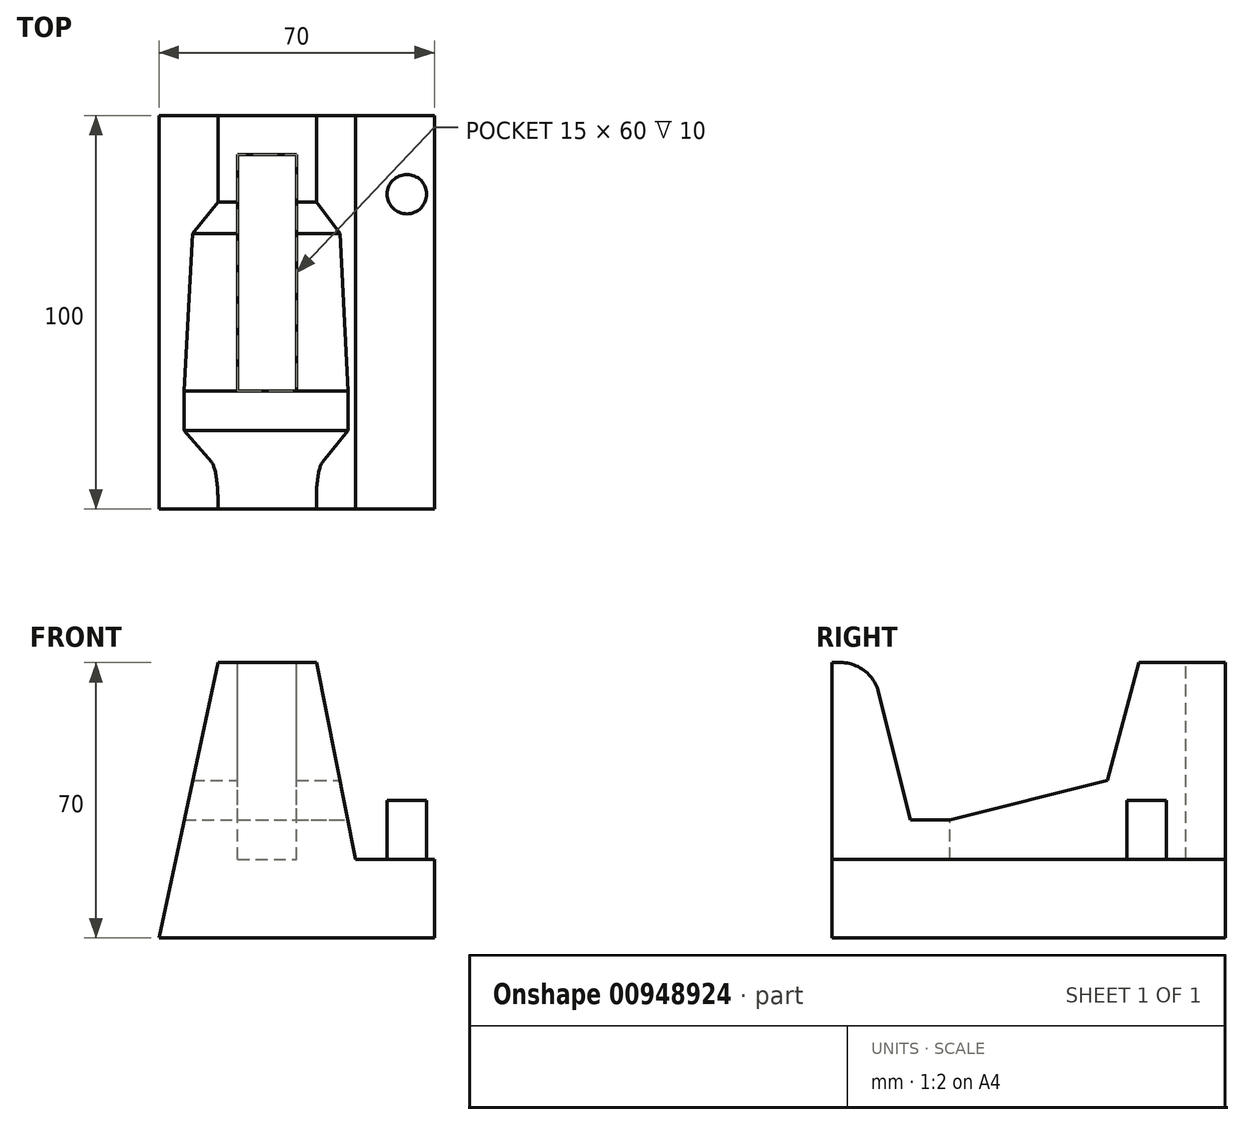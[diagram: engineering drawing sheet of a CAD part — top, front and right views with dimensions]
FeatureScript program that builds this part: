
annotation { "Feature Type Name" : "Feature", "Feature Type Description" : "" }
export const myFeature = defineFeature(function(context is Context, id is Id, definition is map)
    precondition{}
    {
        {
            var Q0;
            Q0=qCreatedBy(makeId("Front.planeOp"),FACE);
            var sketch = newSketch(context, id + "F0", { "sketchPlane" : qUnion([Q0])});
            skLineSegment(sketch, "E0", {"start": v(0, 0) * mm, "end": v(15, 70) * mm});
            skLineSegment(sketch, "E1", {"start": v(15, 70) * mm, "end": v(40, 70) * mm});
            skLineSegment(sketch, "E2", {"start": v(40, 70) * mm, "end": v(50, 20) * mm});
            skLineSegment(sketch, "E3", {"start": v(50, 20) * mm, "end": v(70, 20) * mm});
            skLineSegment(sketch, "E4", {"start": v(70, 20) * mm, "end": v(70, 0) * mm});
            skLineSegment(sketch, "E5", {"start": v(70, 0) * mm, "end": v(0, 0) * mm});
            skSolve(sketch);
        }
        {
            var Q0;
            Q0 = qSketchRegion(id + "F0", true);
            extrude(context, id + "F1", {"entities" : qUnion([Q0]), "oppositeDirection" : true, "depth" : 100 * mm, "offsetDistance" : 25 * mm});
        }
        {
            var Q0;
            Q0=makeQuery(id+"F1.opExtrude","SWEPT_FACE",FACE,{"disambiguationData":[OSD([sQuery(id+"F0.wireOp",EDGE,"E4")])]});
            var sketch = newSketch(context, id + "F2", { "sketchPlane" : qUnion([Q0])});
            skPoint(sketch, "E6.startSnap0", {"position": v(0, 10) * mm});
            skLineSegment(sketch, "E7", {"start": v(10, 70) * mm, "end": v(20, 30) * mm});
            skLineSegment(sketch, "E8", {"start": v(20, 30) * mm, "end": v(30, 30) * mm});
            skLineSegment(sketch, "E9", {"start": v(30, 30) * mm, "end": v(70, 40) * mm});
            skLineSegment(sketch, "E10", {"start": v(70, 40) * mm, "end": v(78.04, 70) * mm});
            skLineSegment(sketch, "E11", {"start": v(78.04, 70) * mm, "end": v(10, 70) * mm});
            skLineSegment(sketch, "E12", {"start": v(70, 40) * mm, "end": v(70, 70) * mm, "construction": true});
            skSolve(sketch);
        }
        {
            var Q0;
            Q0 = qSketchRegion(id + "F2", true);
            extrude(context, id + "F3", {"entities" : qUnion([Q0]), "operationType" : NewBodyOperationType.REMOVE, "endBound" : BoundingType.THROUGH_ALL, "oppositeDirection" : true, "depth" : 25 * mm, "offsetDistance" : 25 * mm});
        }
        {
            var Q0;
            Q0=makeQuery(id+"F3.boolean.opBoolean","COPY",EDGE,{"derivedFrom":makeQuery(id+"F3.opExtrude","SWEPT_EDGE",EDGE,{"disambiguationData":[OSD([sQuery(id+"F2.wireOp",EDGE,"E7"),sQuery(id+"F2.wireOp",EDGE,"E11")])]})});
            var Q1;
            Q1=makeQuery(id+"F3.boolean.opBoolean","COPY",EDGE,{"derivedFrom":makeQuery(id+"F3.opExtrude","SWEPT_EDGE",EDGE,{"disambiguationData":[OSD([sQuery(id+"F2.wireOp",EDGE,"E10"),sQuery(id+"F2.wireOp",EDGE,"E11")])]})});
            fillet(context, id + "F4", {"entities" : qUnion([Q0, Q1]), "radius" : 10 * mm, "tangentPropagation" : true, "allowEdgeOverflow" : false});
        }
        {
            var Q0;
            {var subQ2=sQuery(id+"F0.wireOp",EDGE,"E1");Q0=makeQuery(id+"F3.boolean.opBoolean","SPLIT",FACE,{"disambiguationData":[TD([makeQuery(id+"F3.opExtrude","SWEPT_FACE",FACE,{"disambiguationData":[OSD([sQuery(id+"F2.wireOp",EDGE,"E10")])]})])],"derivedFrom":makeQuery(id+"F1.opExtrude","SWEPT_FACE",FACE,{"disambiguationData":[OSD([subQ2])]})});}
            var sketch = newSketch(context, id + "F5", { "sketchPlane" : qUnion([Q0])});
            skPoint(sketch, "E13.firstSnap0", {"position": v(15, 90) * mm});
            skLineSegment(sketch, "E13.bottom", {"start": v(20, 90) * mm, "end": v(35, 90) * mm});
            skLineSegment(sketch, "E13.top", {"start": v(20, 30) * mm, "end": v(35, 30) * mm});
            skLineSegment(sketch, "E13.left", {"start": v(20, 90) * mm, "end": v(20, 30) * mm});
            skLineSegment(sketch, "E13.right", {"start": v(35, 90) * mm, "end": v(35, 30) * mm});
            skSolve(sketch);
        }
        {
            var Q0;
            Q0 = qSketchRegion(id + "F5", true);
            extrude(context, id + "F6", {"entities" : qUnion([Q0]), "operationType" : NewBodyOperationType.REMOVE, "oppositeDirection" : true, "depth" : 50 * mm, "offsetDistance" : 25 * mm});
        }
        {
            var Q0;
            Q0=makeQuery(id+"F1.opExtrude","SWEPT_FACE",FACE,{"disambiguationData":[OSD([sQuery(id+"F0.wireOp",EDGE,"E3")])]});
            var sketch = newSketch(context, id + "F7", { "sketchPlane" : qUnion([Q0])});
            skCircle(sketch, "E14", {"center": v(63, 80) * mm, "radius": 5 * mm});
            skSolve(sketch);
        }
        {
            var Q0;
            Q0 = qSketchRegion(id + "F7", true);
            extrude(context, id + "F8", {"entities" : qUnion([Q0]), "operationType" : NewBodyOperationType.ADD, "depth" : 15 * mm, "offsetDistance" : 25 * mm});
        }
    });
